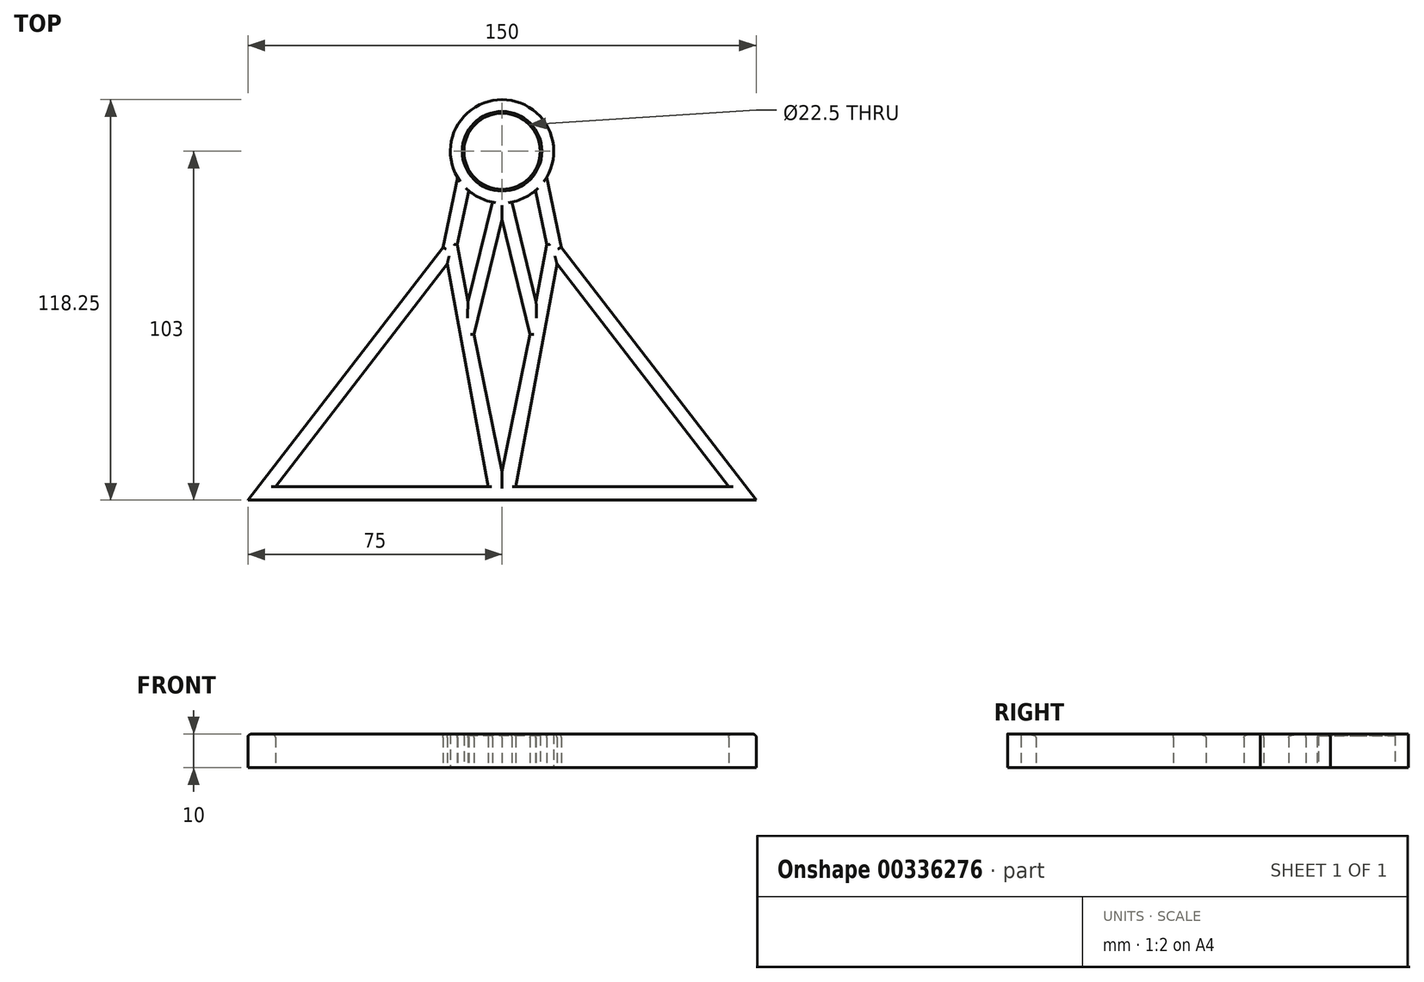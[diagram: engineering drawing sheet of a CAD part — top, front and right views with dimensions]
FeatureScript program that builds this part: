
annotation { "Feature Type Name" : "Feature", "Feature Type Description" : "" }
export const myFeature = defineFeature(function(context is Context, id is Id, definition is map)
    precondition{}
    {
        {
            var Q0;
            Q0=qCreatedBy(makeId("Top.planeOp"),FACE);
            var sketch = newSketch(context, id + "F0", { "sketchPlane" : qUnion([Q0])});
            skLineSegment(sketch, "E0", {"start": v(0, 0) * mm, "end": v(0, -103) * mm, "construction": true});
            skCircle(sketch, "E1", {"center": v(0, 0) * mm, "radius": 11.25 * mm});
            skArc(sketch, "E2", {"start": v(2.86, -14.98) * mm, "mid": v(6.58, -13.76) * mm, "end": v(9.86, -11.63) * mm});
            skLineSegment(sketch, "E3", {"start": v(-75, -103) * mm, "end": v(75, -103) * mm});
            skPoint(sketch, "E4", {"position": v(0, -103) * mm});
            skLineSegment(sketch, "E5", {"start": v(17.48, -28.4) * mm, "end": v(75, -103) * mm});
            skLineSegment(sketch, "E6.0", {"start": v(4.07, -99) * mm, "end": v(66.87, -99) * mm});
            skLineSegment(sketch, "E7", {"start": v(13.2, -27.46) * mm, "end": v(10.06, -44.44) * mm});
            skLineSegment(sketch, "E8.0", {"start": v(16.19, -33.27) * mm, "end": v(4.07, -99) * mm});
            skLineSegment(sketch, "E9", {"start": v(0, -20.12) * mm, "end": v(8.29, -54.05) * mm});
            skLineSegment(sketch, "E10.0", {"start": v(2.86, -14.98) * mm, "end": v(10.06, -44.44) * mm});
            skLineSegment(sketch, "E11", {"start": v(17.48, -28.4) * mm, "end": v(13.13, -7.76) * mm});
            skLineSegment(sketch, "E12.0", {"start": v(13.2, -27.46) * mm, "end": v(9.86, -11.63) * mm});
            skLineSegment(sketch, "E13.0", {"start": v(16.19, -33.27) * mm, "end": v(66.87, -99) * mm});
            skArc(sketch, "E14.trimOffspring", {"start": v(13.13, -7.76) * mm, "mid": v(0, 15.25) * mm, "end": v(-13.13, -7.76) * mm});
            skLineSegment(sketch, "E15.MirrorCS", {"start": v(0, -20.12) * mm, "end": v(-8.29, -54.05) * mm});
            skLineSegment(sketch, "E16.MirrorCS", {"start": v(-2.86, -14.98) * mm, "end": v(-10.06, -44.44) * mm});
            skLineSegment(sketch, "E17.MirrorCS", {"start": v(-13.2, -27.46) * mm, "end": v(-9.86, -11.63) * mm});
            skLineSegment(sketch, "E18.MirrorCS", {"start": v(-13.2, -27.46) * mm, "end": v(-10.06, -44.44) * mm});
            skLineSegment(sketch, "E19.MirrorCS", {"start": v(-17.48, -28.4) * mm, "end": v(-13.13, -7.76) * mm});
            skLineSegment(sketch, "E20.MirrorCS", {"start": v(-17.48, -28.4) * mm, "end": v(-75, -103) * mm});
            skLineSegment(sketch, "E21.MirrorCS", {"start": v(-16.19, -33.27) * mm, "end": v(-66.87, -99) * mm});
            skLineSegment(sketch, "E22.MirrorCS", {"start": v(-16.19, -33.27) * mm, "end": v(-4.07, -99) * mm});
            skLineSegment(sketch, "E23.MirrorCS", {"start": v(-4.07, -99) * mm, "end": v(-66.87, -99) * mm});
            skArc(sketch, "E24.trimOffspring", {"start": v(-9.86, -11.63) * mm, "mid": v(-6.58, -13.76) * mm, "end": v(-2.86, -14.98) * mm});
            skArc(sketch, "E25", {"start": v(-13.13, -7.76) * mm, "mid": v(-11.66, -9.83) * mm, "end": v(-9.86, -11.63) * mm});
            skArc(sketch, "E26", {"start": v(-2.86, -14.98) * mm, "mid": v(0, -15.25) * mm, "end": v(2.86, -14.98) * mm});
            skArc(sketch, "E27", {"start": v(9.86, -11.63) * mm, "mid": v(11.66, -9.83) * mm, "end": v(13.13, -7.76) * mm});
            skLineSegment(sketch, "E28", {"start": v(8.29, -54.05) * mm, "end": v(0, -94.58) * mm});
            skLineSegment(sketch, "E29", {"start": v(0, -94.58) * mm, "end": v(-8.29, -54.05) * mm});
            skSolve(sketch);
        }
        {
            var Q0;
            Q0=makeQuery(id+"F0.imprint","IMPRINT",FACE,{"disambiguationData":[TD([[makeQuery(id+"F0.imprint","IMPRINT",EDGE,{"derivedFrom":sQuery(id+"F0.wireOp",EDGE,"E1")}),-1.0]])]});
            var Q1;
            Q1=makeQuery(id+"F0.imprint","IMPRINT",FACE,{"disambiguationData":[TD([[makeQuery(id+"F0.imprint","IMPRINT",EDGE,{"derivedFrom":sQuery(id+"F0.wireOp",EDGE,"E3")}),1.0]])]});
            extrude(context, id + "F1", {"entities" : qUnion([Q0, Q1]), "depth" : 10 * mm});
        }
        {
            var Q0;
            Q0=makeQuery(id+"F0.imprint","IMPRINT",FACE,{"disambiguationData":[TD([[makeQuery(id+"F0.imprint","IMPRINT",EDGE,{"derivedFrom":sQuery(id+"F0.wireOp",EDGE,"E1")}),-1.0]])]});
            extrude(context, id + "F2", {"entities" : qUnion([Q0]), "operationType" : NewBodyOperationType.ADD, "depth" : 7.1 * mm});
        }
        {
            var Q0;
            Q0=makeQuery(id+"F2.opExtrude","CAP_EDGE",EDGE,{"disambiguationData":[OSD([sQuery(id+"F0.wireOp",EDGE,"E2"),sQuery(id+"F0.wireOp",EDGE,"E14.trimOffspring"),sQuery(id+"F0.wireOp",EDGE,"E24.trimOffspring"),sQuery(id+"F0.wireOp",EDGE,"E25"),sQuery(id+"F0.wireOp",EDGE,"E26"),sQuery(id+"F0.wireOp",EDGE,"E27")])],"isStart":false});
            var Q1;
            Q1=makeQuery(id+"F2.opExtrude","CAP_EDGE",EDGE,{"disambiguationData":[OSD([sQuery(id+"F0.wireOp",EDGE,"E2"),sQuery(id+"F0.wireOp",EDGE,"E14.trimOffspring"),sQuery(id+"F0.wireOp",EDGE,"E24.trimOffspring"),sQuery(id+"F0.wireOp",EDGE,"E25"),sQuery(id+"F0.wireOp",EDGE,"E26"),sQuery(id+"F0.wireOp",EDGE,"E27")])],"isStart":true});
            var Q2;
            Q2=makeQuery(id+"F1.opExtrude","CAP_EDGE",EDGE,{"disambiguationData":[OSD([sQuery(id+"F0.wireOp",EDGE,"E19.MirrorCS")])],"isStart":false});
            var Q3;
            Q3=makeQuery(id+"F1.opExtrude","CAP_EDGE",EDGE,{"disambiguationData":[OSD([sQuery(id+"F0.wireOp",EDGE,"E17.MirrorCS")])],"isStart":false});
            var Q4;
            Q4=makeQuery(id+"F1.opExtrude","CAP_EDGE",EDGE,{"disambiguationData":[OSD([sQuery(id+"F0.wireOp",EDGE,"E18.MirrorCS")])],"isStart":false});
            var Q5;
            Q5=makeQuery(id+"F1.opExtrude","CAP_EDGE",EDGE,{"disambiguationData":[OSD([sQuery(id+"F0.wireOp",EDGE,"E20.MirrorCS")])],"isStart":false});
            var Q6;
            Q6=makeQuery(id+"F1.opExtrude","CAP_EDGE",EDGE,{"disambiguationData":[OSD([sQuery(id+"F0.wireOp",EDGE,"E21.MirrorCS")])],"isStart":false});
            var Q7;
            Q7=makeQuery(id+"F1.opExtrude","CAP_EDGE",EDGE,{"disambiguationData":[OSD([sQuery(id+"F0.wireOp",EDGE,"E22.MirrorCS")])],"isStart":false});
            var Q8;
            Q8=makeQuery(id+"F1.opExtrude","CAP_EDGE",EDGE,{"disambiguationData":[OSD([sQuery(id+"F0.wireOp",EDGE,"E16.MirrorCS")])],"isStart":false});
            var Q9;
            Q9=makeQuery(id+"F1.opExtrude","CAP_EDGE",EDGE,{"disambiguationData":[OSD([sQuery(id+"F0.wireOp",EDGE,"E10.0")])],"isStart":false});
            var Q10;
            Q10=makeQuery(id+"F1.opExtrude","CAP_EDGE",EDGE,{"disambiguationData":[OSD([sQuery(id+"F0.wireOp",EDGE,"E12.0")])],"isStart":false});
            var Q11;
            Q11=makeQuery(id+"F1.opExtrude","CAP_EDGE",EDGE,{"disambiguationData":[OSD([sQuery(id+"F0.wireOp",EDGE,"E7")])],"isStart":false});
            var Q12;
            Q12=makeQuery(id+"F1.opExtrude","CAP_EDGE",EDGE,{"disambiguationData":[OSD([sQuery(id+"F0.wireOp",EDGE,"E11")])],"isStart":false});
            var Q13;
            Q13=makeQuery(id+"F1.opExtrude","CAP_EDGE",EDGE,{"disambiguationData":[OSD([sQuery(id+"F0.wireOp",EDGE,"E5")])],"isStart":false});
            var Q14;
            Q14=makeQuery(id+"F1.opExtrude","CAP_EDGE",EDGE,{"disambiguationData":[OSD([sQuery(id+"F0.wireOp",EDGE,"E13.0")])],"isStart":false});
            var Q15;
            Q15=makeQuery(id+"F1.opExtrude","CAP_EDGE",EDGE,{"disambiguationData":[OSD([sQuery(id+"F0.wireOp",EDGE,"E8.0")])],"isStart":false});
            var Q16;
            Q16=makeQuery(id+"F1.opExtrude","CAP_EDGE",EDGE,{"disambiguationData":[OSD([sQuery(id+"F0.wireOp",EDGE,"E15.MirrorCS")])],"isStart":false});
            var Q17;
            Q17=makeQuery(id+"F1.opExtrude","CAP_EDGE",EDGE,{"disambiguationData":[OSD([sQuery(id+"F0.wireOp",EDGE,"25fc83b3-86e4-4527-ae88-7d0f36e44f400.MirrorCS")])],"isStart":false});
            var Q18;
            Q18=makeQuery(id+"F1.opExtrude","CAP_EDGE",EDGE,{"disambiguationData":[OSD([sQuery(id+"F0.wireOp",EDGE,"dfd69ec2-366f-4c7d-84fe-dc5a4019acf0.trimOffspring")])],"isStart":false});
            var Q19;
            Q19=makeQuery(id+"F1.opExtrude","CAP_EDGE",EDGE,{"disambiguationData":[OSD([sQuery(id+"F0.wireOp",EDGE,"E29")])],"isStart":false});
            var Q20;
            Q20=makeQuery(id+"F1.opExtrude","CAP_EDGE",EDGE,{"disambiguationData":[OSD([sQuery(id+"F0.wireOp",EDGE,"E28")])],"isStart":false});
            fillet(context, id + "F3", {"entities" : qUnion([Q0, Q1, Q2, Q3, Q4, Q5, Q6, Q7, Q8, Q9, Q10, Q11, Q12, Q13, Q14, Q15, Q16, Q17, Q18, Q19, Q20]), "radius" : 1 * mm, "tangentPropagation" : true, "allowEdgeOverflow" : false});
        }
        {
            var Q0;
            Q0=makeQuery(id+"F1.opExtrude","CAP_EDGE",EDGE,{"disambiguationData":[OSD([sQuery(id+"F0.wireOp",EDGE,"E9")])],"isStart":false});
            fillet(context, id + "F4", {"entities" : qUnion([Q0]), "radius" : 1 * mm, "tangentPropagation" : true, "allowEdgeOverflow" : false});
        }
        {
            var Q0;
            Q0=makeQuery(id+"F1.opExtrude","CAP_EDGE",EDGE,{"disambiguationData":[OSD([sQuery(id+"F0.wireOp",EDGE,"E1")])],"isStart":false});
            chamfer(context, id + "F5", {"entities" : qUnion([Q0]), "width" : 0.5 * mm, "tangentPropagation" : true});
        }
    });
